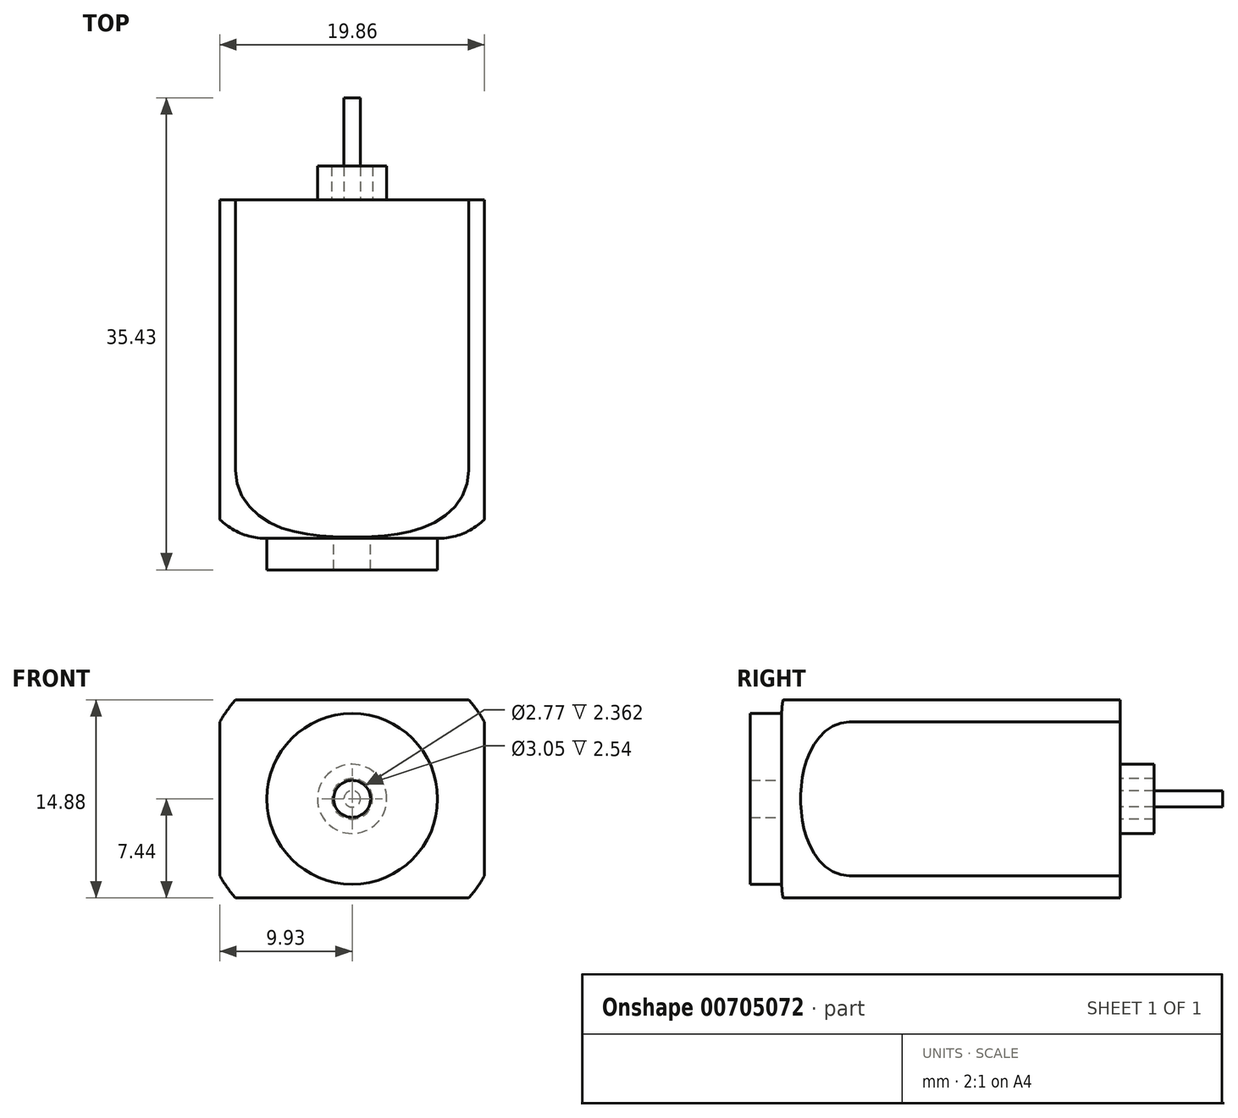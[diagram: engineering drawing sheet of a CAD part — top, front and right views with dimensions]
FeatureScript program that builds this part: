
annotation { "Feature Type Name" : "Feature", "Feature Type Description" : "" }
export const myFeature = defineFeature(function(context is Context, id is Id, definition is map)
    precondition{}
    {
        {
            var Q0;
            Q0=qCreatedBy(makeId("Front.planeOp"),FACE);
            var sketch = newSketch(context, id + "F0", { "sketchPlane" : qUnion([Q0])});
            skCircle(sketch, "E0", {"center": v(0, 0) * mm, "radius": 11.49 * mm});
            skLineSegment(sketch, "E1.bottom", {"start": v(9.93, 7.44) * mm, "end": v(-9.93, 7.44) * mm});
            skLineSegment(sketch, "E1.top", {"start": v(9.93, -7.44) * mm, "end": v(-9.93, -7.44) * mm});
            skLineSegment(sketch, "E1.left", {"start": v(9.93, 7.44) * mm, "end": v(9.93, -7.44) * mm});
            skLineSegment(sketch, "E1.right", {"start": v(-9.93, 7.44) * mm, "end": v(-9.93, -7.44) * mm});
            skSolve(sketch);
        }
        {
            var Q0;
            Q0=makeQuery(id+"F0.imprint","IMPRINT",FACE,{"disambiguationData":[TD([[makeQuery(id+"F0.imprint","IMPRINT",EDGE,{"derivedFrom":sQuery(id+"F0.wireOp",EDGE,"E0")}),1.0]])]});
            var Q1;
            {var subQ0=sQuery(id+"F0.wireOp",EDGE,"7VfKRUgh-YDTa-teSQ-S0Gt-cZazTemTm8sU");Q1=makeQuery(id+"F0.imprint","IMPRINT",FACE,{"disambiguationData":[TD([[makeQuery(id+"F0.imprint","IMPRINT",EDGE,{"derivedFrom":subQ0}),-1.0]])]});}
            extrude(context, id + "F1", {"entities" : qUnion([Q0, Q1]), "depth" : 25.4 * mm, "offsetDistance" : 25.4 * mm});
        }
        {
            var Q0;
            {var subQ0=sQuery(id+"F0.wireOp",EDGE,"E0");Q0=makeQuery(id+"F1.opExtrude","CAP_EDGE",EDGE,{"disambiguationData":[OSD([subQ0]),TDD([makeQuery(id+"F0.imprint","IMPRINT",EDGE,{"disambiguationData":[TD([[makeQuery(id+"F0.imprint","INTERSECT",VERTEX,{"disambiguationData":[OD(1.0)],"derivedFrom":[subQ0,sQuery(id+"F0.wireOp",EDGE,"E1.bottom")]}),-1.0]])],"derivedFrom":subQ0})])],"isStart":false});}
            fillet(context, id + "F2", {"entities" : qUnion([Q0]), "radius" : 5.08 * mm, "tangentPropagation" : true, "allowEdgeOverflow" : false});
        }
        {
            var Q0;
            Q0=makeQuery(id+"F1.opExtrude","CAP_FACE",FACE,{"disambiguationData":[OSD([sQuery(id+"F0.wireOp",EDGE,"E0"),sQuery(id+"F0.wireOp",EDGE,"E1.bottom"),sQuery(id+"F0.wireOp",EDGE,"E1.top"),sQuery(id+"F0.wireOp",EDGE,"E1.left"),sQuery(id+"F0.wireOp",EDGE,"E1.right")])],"isStart":false});
            var sketch = newSketch(context, id + "F3", { "sketchPlane" : qUnion([Q0])});
            skCircle(sketch, "E2", {"center": v(0, 0) * mm, "radius": 1.39 * mm});
            skSolve(sketch);
        }
        {
            var Q0;
            Q0=makeQuery(id+"F3.imprint","IMPRINT",FACE,{"disambiguationData":[TD([[makeQuery(id+"F3.imprint","IMPRINT",EDGE,{"derivedFrom":sQuery(id+"F3.wireOp",EDGE,"E2")}),-1.0]])]});
            extrude(context, id + "F4", {"entities" : qUnion([Q0]), "operationType" : NewBodyOperationType.ADD, "depth" : 2.36 * mm, "offsetDistance" : 25.4 * mm});
        }
        {
            var Q0;
            {var subQ1=sQuery(id+"F0.wireOp",EDGE,"E0");var subQ9=sQuery(id+"F0.wireOp",EDGE,"E1.bottom");var subQ12=makeQuery(id+"F0.imprint","INTERSECT",VERTEX,{"disambiguationData":[OD(0.0)],"derivedFrom":[subQ1,subQ9]});Q0=makeQuery(id+"F0.imprint","IMPRINT",FACE,{"disambiguationData":[TD([[makeQuery(id+"F0.imprint","IMPRINT",EDGE,{"disambiguationData":[TD([[subQ12,1.0]])],"derivedFrom":subQ1}),1.0]])]});}
            var sketch = newSketch(context, id + "F5", { "sketchPlane" : qUnion([Q0])});
            skCircle(sketch, "E3", {"center": v(0, 0) * mm, "radius": 2.6 * mm});
            skCircle(sketch, "E4", {"center": v(0, 0) * mm, "radius": 1.53 * mm});
            skSolve(sketch);
        }
        {
            var Q0;
            Q0 = qSketchRegion(id + "F5", true);
            extrude(context, id + "F6", {"entities" : qUnion([Q0]), "operationType" : NewBodyOperationType.ADD, "oppositeDirection" : true, "depth" : 2.54 * mm, "offsetDistance" : 25.4 * mm});
        }
        {
            var Q0;
            Q0=qCreatedBy(makeId("Front.planeOp"),FACE);
            var sketch = newSketch(context, id + "F7", { "sketchPlane" : qUnion([Q0])});
            skCircle(sketch, "E5", {"center": v(0, 0) * mm, "radius": 0.61 * mm});
            skSolve(sketch);
        }
        {
            var Q0;
            Q0 = qSketchRegion(id + "F7", true);
            extrude(context, id + "F8", {"entities" : qUnion([Q0]), "operationType" : NewBodyOperationType.ADD, "oppositeDirection" : true, "depth" : 7.67 * mm, "offsetDistance" : 25.4 * mm});
        }
    });
